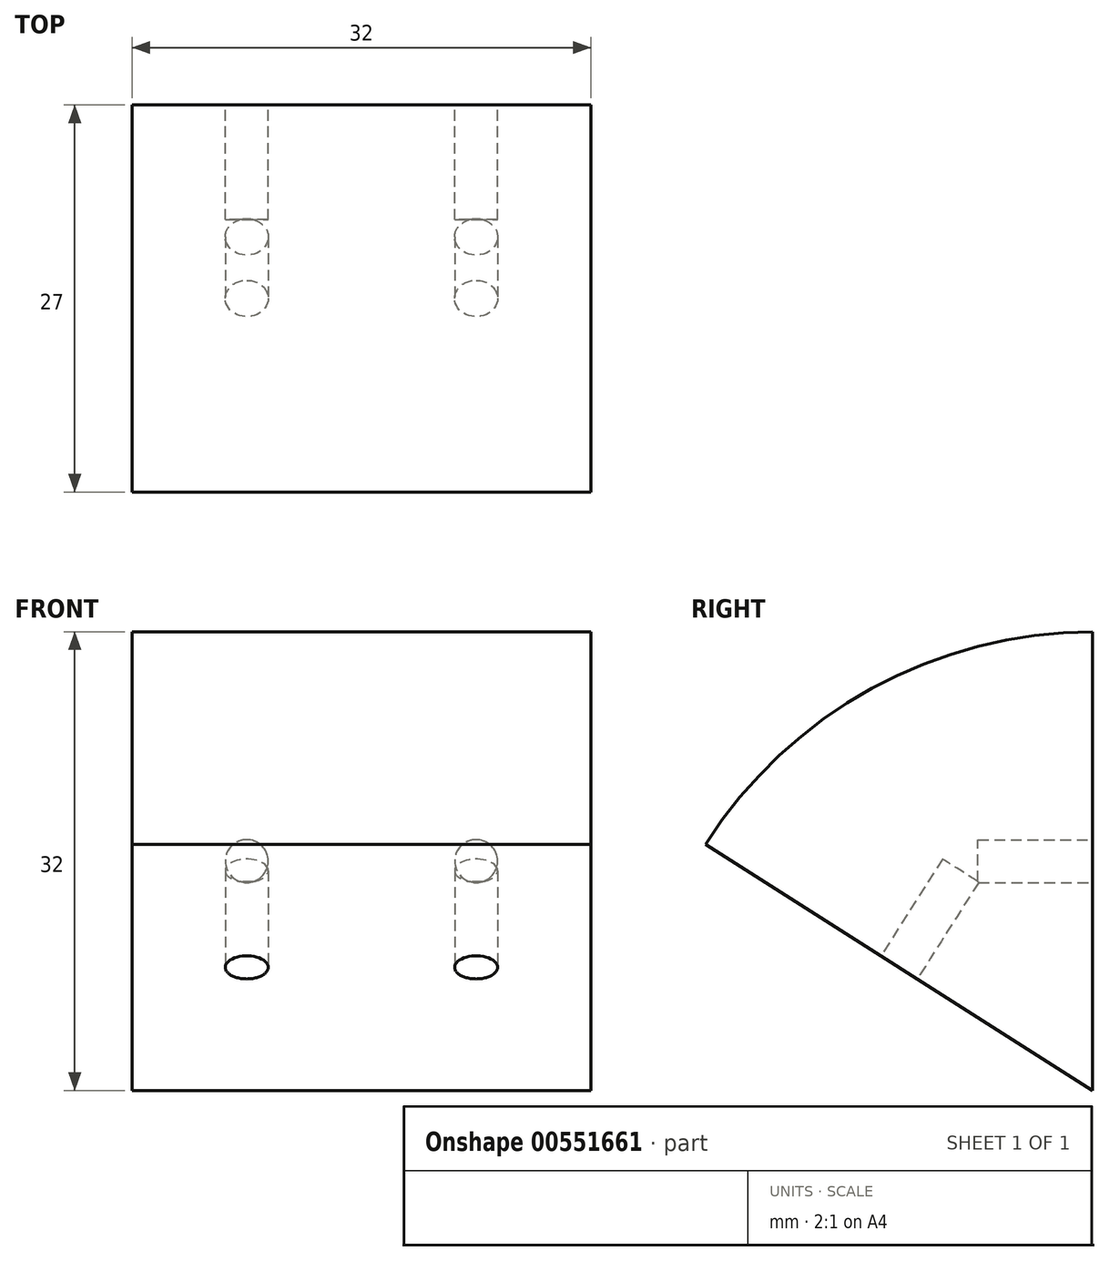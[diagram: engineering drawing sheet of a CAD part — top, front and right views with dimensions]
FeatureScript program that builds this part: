
annotation { "Feature Type Name" : "Feature", "Feature Type Description" : "" }
export const myFeature = defineFeature(function(context is Context, id is Id, definition is map)
    precondition{}
    {
        {
            var Q0;
            Q0=qCreatedBy(makeId("Front.planeOp"),FACE);
            var sketch = newSketch(context, id + "F0", { "sketchPlane" : qUnion([Q0])});
            skLineSegment(sketch, "E0.bottom", {"start": v(-17.22, 24.92) * mm, "end": v(14.78, 24.92) * mm});
            skLineSegment(sketch, "E0.top", {"start": v(-17.22, -7.08) * mm, "end": v(14.78, -7.08) * mm});
            skLineSegment(sketch, "E0.left", {"start": v(-17.22, 24.92) * mm, "end": v(-17.22, -7.08) * mm});
            skLineSegment(sketch, "E0.right", {"start": v(14.78, 24.92) * mm, "end": v(14.78, -7.08) * mm});
            skSolve(sketch);
        }
        {
            var Q0;
            Q0=makeQuery(id+"F0.imprint","IMPRINT",FACE,{"disambiguationData":[TD([[makeQuery(id+"F0.imprint","IMPRINT",EDGE,{"derivedFrom":sQuery(id+"F0.wireOp",EDGE,"E0.bottom")}),-1.0]])]});
            var Q1;
            Q1=sQuery(id+"F0.wireOp",EDGE,"E0.top");
            revolve(context, id + "F1", {"entities" : qUnion([Q0]), "axis" : qUnion([Q1]), "revolveType" : RevolveType.ONE_DIRECTION, "angle" : 57.53 * degree});
        }
        {
            var Q0;
            Q0=makeQuery(id+"F1.opRevolve","CAP_FACE",FACE,{"disambiguationData":[OSD([sQuery(id+"F0.wireOp",EDGE,"E0.bottom"),sQuery(id+"F0.wireOp",EDGE,"E0.top"),sQuery(id+"F0.wireOp",EDGE,"E0.left"),sQuery(id+"F0.wireOp",EDGE,"E0.right")])],"isStart":true});
            var sketch = newSketch(context, id + "F2", { "sketchPlane" : qUnion([Q0])});
            skCircle(sketch, "E1", {"center": v(-6.78, 8.92) * mm, "radius": 1.5 * mm});
            skPoint(sketch, "E1.centerSnap0", {"position": v(-14.78, 8.92) * mm});
            skCircle(sketch, "E2.1.0.0", {"center": v(9.22, 8.92) * mm, "radius": 1.5 * mm});
            skLineSegment(sketch, "E2.direction1", {"start": v(-6.78, 8.92) * mm, "end": v(9.22, 8.92) * mm, "construction": true});
            skSolve(sketch);
        }
        {
            var Q0;
            Q0=makeQuery(id+"F2.imprint","IMPRINT",FACE,{"disambiguationData":[TD([[makeQuery(id+"F2.imprint","IMPRINT",EDGE,{"derivedFrom":sQuery(id+"F2.wireOp",EDGE,"E1")}),1.0]])]});
            var Q1;
            Q1=makeQuery(id+"F2.imprint","IMPRINT",FACE,{"disambiguationData":[TD([[makeQuery(id+"F2.imprint","IMPRINT",EDGE,{"derivedFrom":sQuery(id+"F2.wireOp",EDGE,"E2.1.0.0")}),1.0]])]});
            var Q2;
            Q2=sQuery(id+"F2.wireOp",EDGE,"E1");
            var Q3;
            Q3=sQuery(id+"F2.wireOp",EDGE,"E2.1.0.0");
            extrude(context, id + "F3", {"entities" : qUnion([Q0, Q1]), "operationType" : NewBodyOperationType.REMOVE, "surfaceEntities" : qUnion([Q2, Q3]), "oppositeDirection" : true, "depth" : 8 * mm, "offsetDistance" : 25 * mm});
        }
        {
            var Q0;
            Q0=makeQuery(id+"F1.opRevolve","CAP_FACE",FACE,{"disambiguationData":[OSD([sQuery(id+"F0.wireOp",EDGE,"E0.bottom"),sQuery(id+"F0.wireOp",EDGE,"E0.top"),sQuery(id+"F0.wireOp",EDGE,"E0.left"),sQuery(id+"F0.wireOp",EDGE,"E0.right")])],"isStart":false});
            var sketch = newSketch(context, id + "F4", { "sketchPlane" : qUnion([Q0])});
            skCircle(sketch, "E3", {"center": v(6.78, 12.2) * mm, "radius": 1.5 * mm});
            skCircle(sketch, "E4.1.0.0", {"center": v(-9.22, 12.2) * mm, "radius": 1.5 * mm});
            skLineSegment(sketch, "E4.direction1", {"start": v(6.78, 12.2) * mm, "end": v(-9.22, 12.2) * mm, "construction": true});
            skSolve(sketch);
        }
        {
            var Q0;
            Q0=makeQuery(id+"F4.imprint","IMPRINT",FACE,{"disambiguationData":[TD([[makeQuery(id+"F4.imprint","IMPRINT",EDGE,{"derivedFrom":sQuery(id+"F4.wireOp",EDGE,"E3")}),1.0]])]});
            var Q1;
            Q1=makeQuery(id+"F4.imprint","IMPRINT",FACE,{"disambiguationData":[TD([[makeQuery(id+"F4.imprint","IMPRINT",EDGE,{"derivedFrom":sQuery(id+"F4.wireOp",EDGE,"E4.1.0.0")}),1.0]])]});
            extrude(context, id + "F5", {"entities" : qUnion([Q0, Q1]), "operationType" : NewBodyOperationType.REMOVE, "oppositeDirection" : true, "depth" : 8 * mm, "offsetDistance" : 25 * mm});
        }
    });
